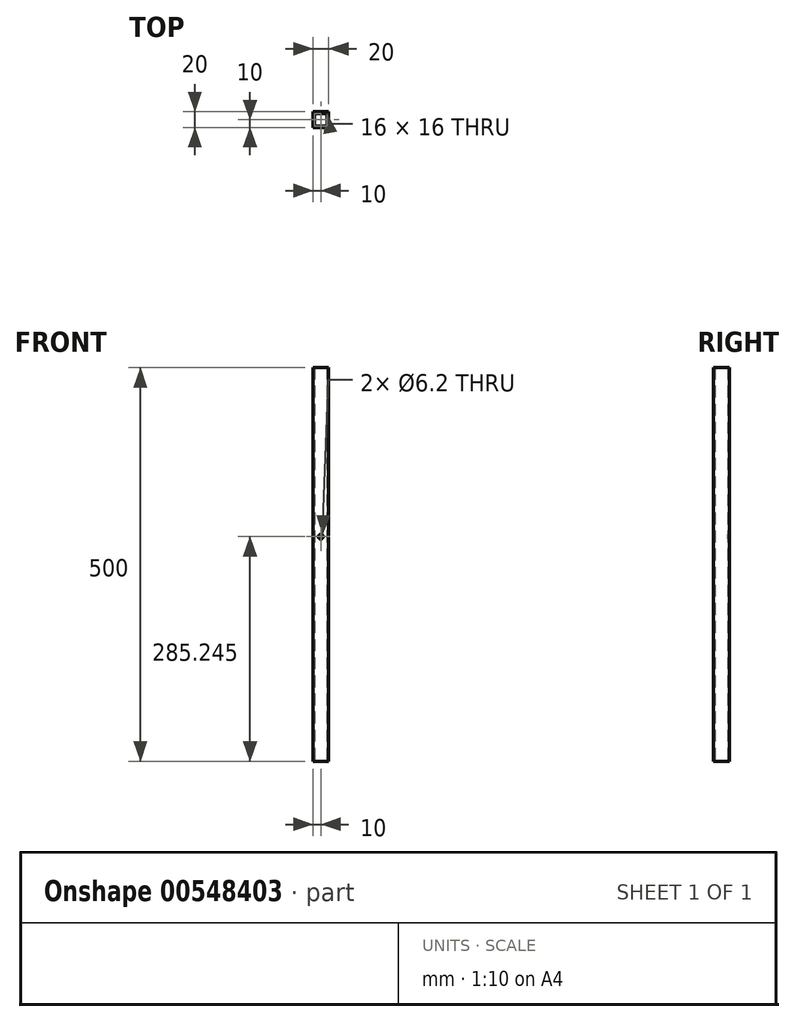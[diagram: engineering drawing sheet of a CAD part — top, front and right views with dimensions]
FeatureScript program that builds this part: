
annotation { "Feature Type Name" : "Feature", "Feature Type Description" : "" }
export const myFeature = defineFeature(function(context is Context, id is Id, definition is map)
    precondition{}
    {
        {
            var Q0;
            Q0=qCreatedBy(makeId("Top.planeOp"),FACE);
            var sketch = newSketch(context, id + "F0", { "sketchPlane" : qUnion([Q0])});
            skLineSegment(sketch, "E0.bottom", {"start": v(10, -10) * mm, "end": v(-10, -10) * mm});
            skLineSegment(sketch, "E0.top", {"start": v(10, 10) * mm, "end": v(-10, 10) * mm});
            skLineSegment(sketch, "E0.left", {"start": v(10, -10) * mm, "end": v(10, 10) * mm});
            skLineSegment(sketch, "E0.right", {"start": v(-10, -10) * mm, "end": v(-10, 10) * mm});
            skPoint(sketch, "E0.middle", {"position": v(0, 0) * mm});
            skLineSegment(sketch, "E1.0", {"start": v(8, -8) * mm, "end": v(8, 8) * mm});
            skLineSegment(sketch, "E1.1", {"start": v(8, -8) * mm, "end": v(-8, -8) * mm});
            skLineSegment(sketch, "E1.2", {"start": v(-8, -8) * mm, "end": v(-8, 8) * mm});
            skLineSegment(sketch, "E1.3", {"start": v(8, 8) * mm, "end": v(-8, 8) * mm});
            skSolve(sketch);
        }
        {
            var Q0;
            Q0=makeQuery(id+"F0.imprint","IMPRINT",FACE,{"disambiguationData":[TD([[makeQuery(id+"F0.imprint","IMPRINT",EDGE,{"derivedFrom":sQuery(id+"F0.wireOp",EDGE,"E0.bottom")}),-1.0]])]});
            extrude(context, id + "F1", {"entities" : qUnion([Q0]), "depth" : 500 * mm, "offsetDistance" : 25.4 * mm});
        }
        {
            var Q0;
            Q0=makeQuery(id+"F1.opExtrude","SWEPT_FACE",FACE,{"disambiguationData":[OSD([sQuery(id+"F0.wireOp",EDGE,"E0.bottom")])]});
            var sketch = newSketch(context, id + "F2", { "sketchPlane" : qUnion([Q0])});
            skCircle(sketch, "E2", {"center": v(0, 285.24) * mm, "radius": 3.1 * mm});
            skSolve(sketch);
        }
        {
            var Q0;
            Q0=makeQuery(id+"F2.imprint","IMPRINT",FACE,{"disambiguationData":[TD([[makeQuery(id+"F2.imprint","IMPRINT",EDGE,{"derivedFrom":sQuery(id+"F2.wireOp",EDGE,"E2")}),1.0]])]});
            var Q1;
            Q1=sQuery(id+"F2.wireOp",EDGE,"E2");
            extrude(context, id + "F3", {"entities" : qUnion([Q0]), "operationType" : NewBodyOperationType.REMOVE, "surfaceEntities" : qUnion([Q1]), "oppositeDirection" : true, "depth" : 39.37 * mm, "offsetDistance" : 25.4 * mm});
        }
    });
